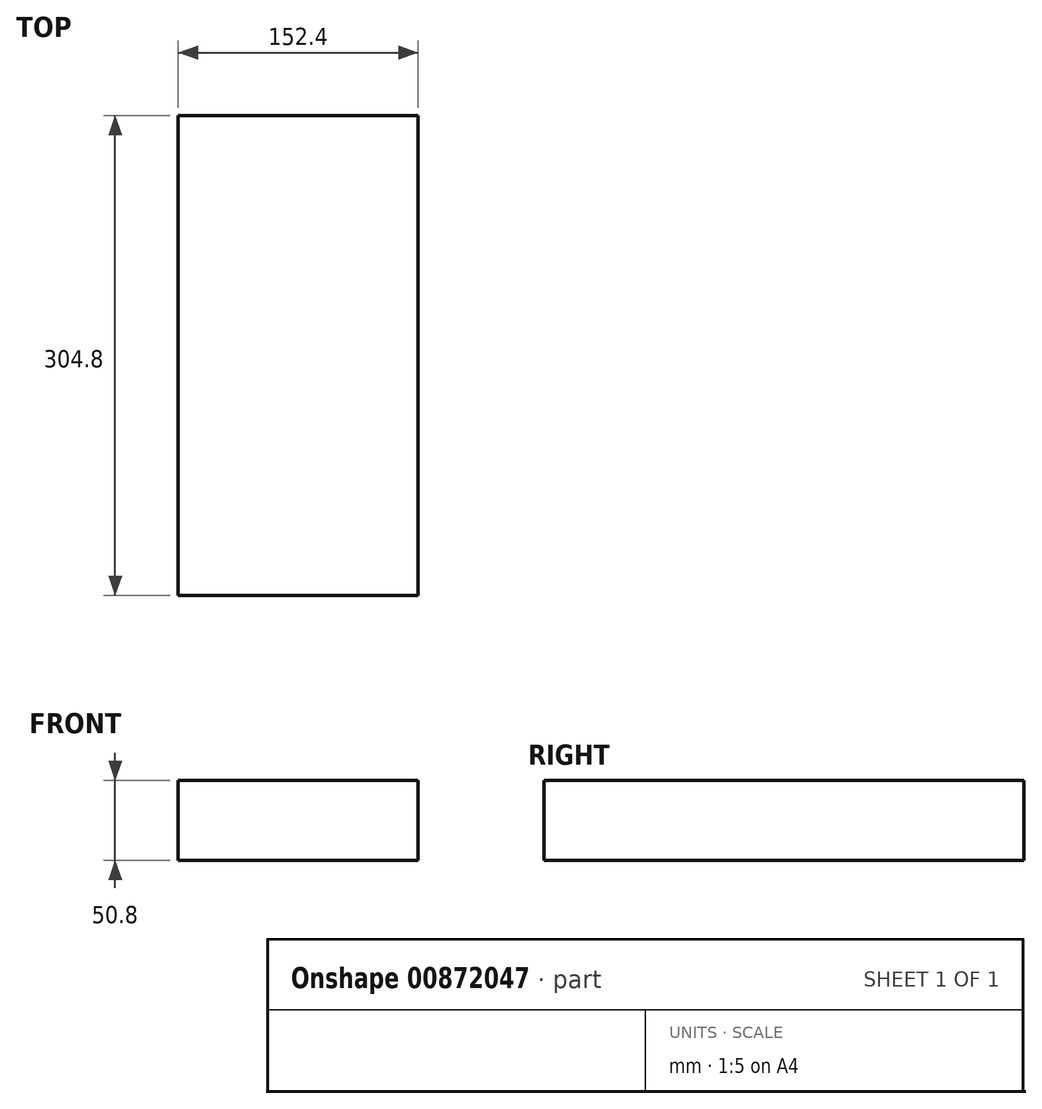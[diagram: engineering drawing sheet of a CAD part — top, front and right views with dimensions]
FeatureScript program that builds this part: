
annotation { "Feature Type Name" : "Feature", "Feature Type Description" : "" }
export const myFeature = defineFeature(function(context is Context, id is Id, definition is map)
    precondition{}
    {
        {
            var Q0;
            Q0=qCreatedBy(makeId("Front.planeOp"),FACE);
            var sketch = newSketch(context, id + "F0", { "sketchPlane" : qUnion([Q0])});
            skLineSegment(sketch, "E0.bottom", {"start": v(-76.2, 25.4) * mm, "end": v(76.2, 25.4) * mm});
            skLineSegment(sketch, "E0.top", {"start": v(-76.2, -25.4) * mm, "end": v(76.2, -25.4) * mm});
            skLineSegment(sketch, "E0.left", {"start": v(-76.2, 25.4) * mm, "end": v(-76.2, -25.4) * mm});
            skLineSegment(sketch, "E0.right", {"start": v(76.2, 25.4) * mm, "end": v(76.2, -25.4) * mm});
            skSolve(sketch);
        }
        {
            var Q0;
            Q0 = qSketchRegion(id + "F0", true);
            extrude(context, id + "F1", {"entities" : qUnion([Q0]), "depth" : 304.8 * mm, "offsetDistance" : 25.4 * mm});
        }
    });
